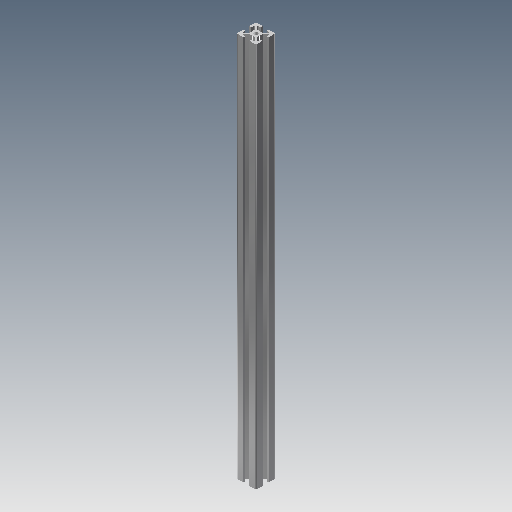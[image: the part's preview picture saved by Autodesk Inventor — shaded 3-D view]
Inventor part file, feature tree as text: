
AUTODESK INVENTOR PART (.ipt)
format: ipt  version: 2017 (Build 210142000, 142)  size: 166,912 bytes
history: native  units: mm
features: extrude x1, sketch x1
ambient origin geometry x8: Origin, YZ Plane, XZ Plane, XY Plane, X Axis, Y Axis, Z Axis, Center Point
bodies: Solid1 (feature_tree)
feature tree (2):
  extrude  "Extrusion1"  [1 undecoded]
  sketch  "Sketch1"  dims[d0=400.0mm d1=0.0mm]
note: 1 required parameter value undecoded (feature->parameter linkage not recoverable at this tier; creation-order binding heuristic only, values carry confidence <= 0.55)
